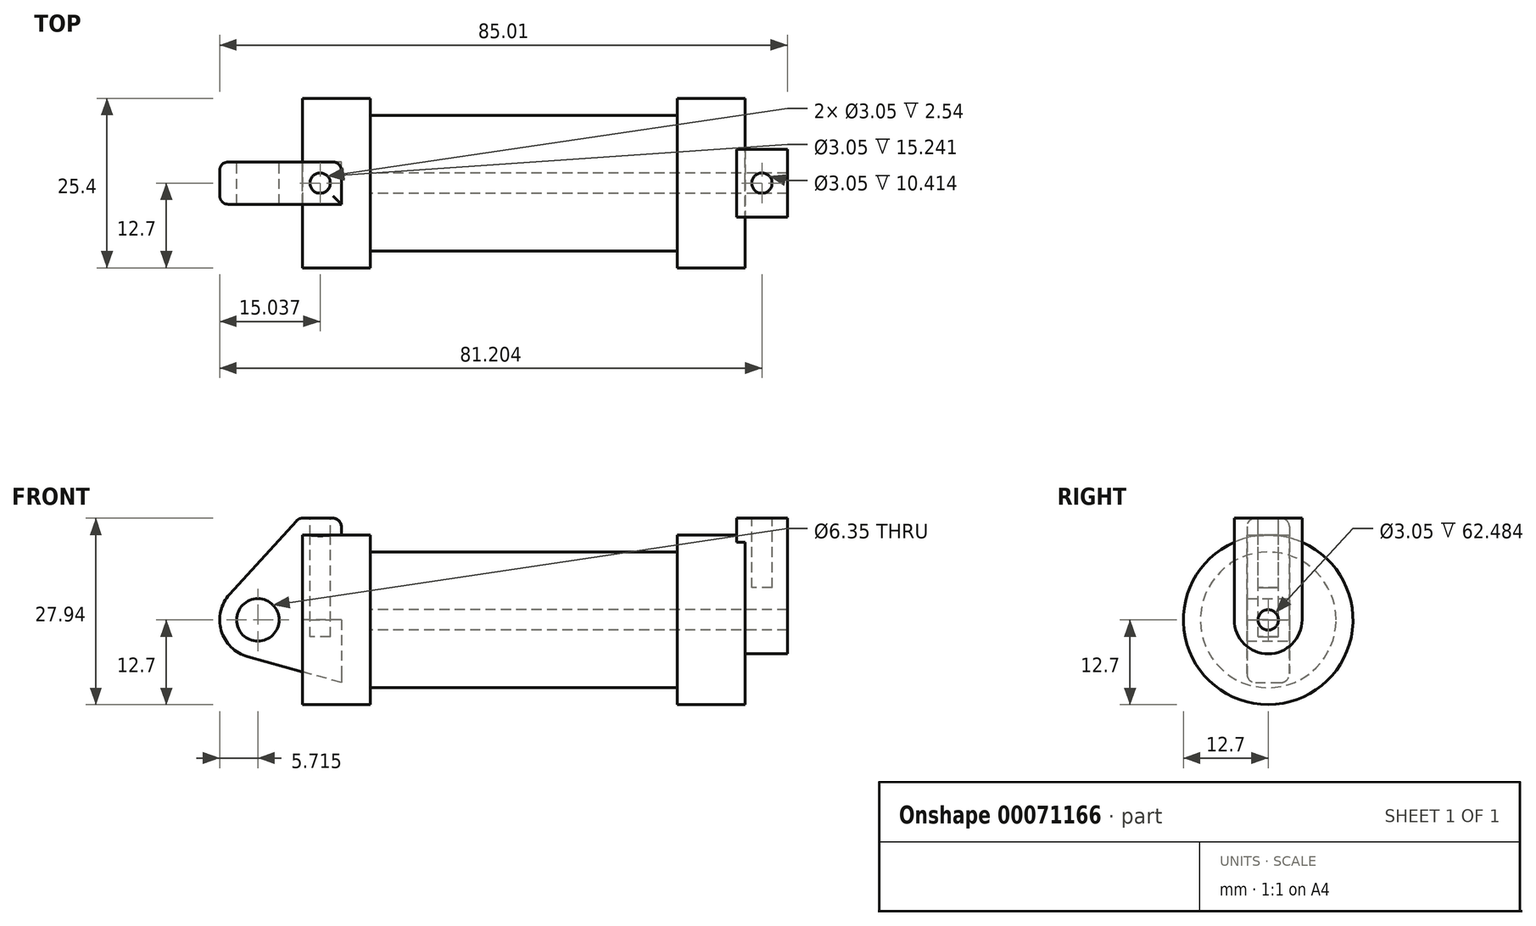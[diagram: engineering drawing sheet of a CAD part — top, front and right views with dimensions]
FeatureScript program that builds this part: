
annotation { "Feature Type Name" : "Feature", "Feature Type Description" : "" }
export const myFeature = defineFeature(function(context is Context, id is Id, definition is map)
    precondition{}
    {
        {
            var Q0;
            Q0=qCreatedBy(makeId("Front.planeOp"),FACE);
            var sketch = newSketch(context, id + "F0", { "sketchPlane" : qUnion([Q0])});
            skLineSegment(sketch, "E0", {"start": v(0, 0) * mm, "end": v(0, 12.7) * mm});
            skLineSegment(sketch, "E1", {"start": v(0, 12.7) * mm, "end": v(10.16, 12.7) * mm});
            skLineSegment(sketch, "E2", {"start": v(10.16, 12.7) * mm, "end": v(10.16, 10.16) * mm});
            skLineSegment(sketch, "E3", {"start": v(10.16, 10.16) * mm, "end": v(56.13, 10.16) * mm});
            skLineSegment(sketch, "E4", {"start": v(56.13, 10.16) * mm, "end": v(56.13, 12.7) * mm});
            skLineSegment(sketch, "E5", {"start": v(56.13, 12.7) * mm, "end": v(66.3, 12.7) * mm});
            skLineSegment(sketch, "E6", {"start": v(66.3, 12.7) * mm, "end": v(66.3, 0) * mm});
            skLineSegment(sketch, "E7", {"start": v(66.3, 0) * mm, "end": v(0, 0) * mm});
            skLineSegment(sketch, "E8", {"start": v(5.84, 15.24) * mm, "end": v(-0.5, 15.24) * mm});
            skLineSegment(sketch, "E9", {"start": v(-0.5, 15.24) * mm, "end": v(-10.88, 3.85) * mm});
            skLineSegment(sketch, "E10", {"start": v(0, 0) * mm, "end": v(-6.65, 0) * mm});
            skCircle(sketch, "E11", {"center": v(-6.65, 0) * mm, "radius": 5.72 * mm});
            skCircle(sketch, "E12", {"center": v(-6.65, 0) * mm, "radius": 3.18 * mm});
            skLineSegment(sketch, "E13", {"start": v(5.84, 15.24) * mm, "end": v(5.84, -9.4) * mm});
            skLineSegment(sketch, "E14", {"start": v(5.84, -9.4) * mm, "end": v(-8.18, -5.5) * mm});
            skSolve(sketch);
        }
        {
            var Q0;
            {var subQ0=sQuery(id+"F0.wireOp",EDGE,"E0");Q0=makeQuery(id+"F0.imprint","IMPRINT",FACE,{"disambiguationData":[TD([[makeQuery(id+"F0.imprint","IMPRINT",EDGE,{"derivedFrom":subQ0}),-1.0]])]});}
            var Q1;
            {var subQ0=sQuery(id+"F0.wireOp",EDGE,"E2");Q1=makeQuery(id+"F0.imprint","IMPRINT",FACE,{"disambiguationData":[TD([[makeQuery(id+"F0.imprint","IMPRINT",EDGE,{"derivedFrom":subQ0}),-1.0]])]});}
            var Q2;
            Q2=sQuery(id+"F0.wireOp",EDGE,"E7");
            revolve(context, id + "F1", {"entities" : qUnion([Q0, Q1]), "axis" : qUnion([Q2]), "revolveType" : RevolveType.FULL});
        }
        {
            var Q0;
            {var subQ3=sQuery(id+"F0.wireOp",EDGE,"E0");Q0=makeQuery(id+"F0.imprint","IMPRINT",FACE,{"disambiguationData":[TD([[makeQuery(id+"F0.imprint","IMPRINT",EDGE,{"derivedFrom":subQ3}),1.0]])]});}
            var Q1;
            {var subQ4=sQuery(id+"F0.wireOp",EDGE,"E12");Q1=makeQuery(id+"F0.imprint","IMPRINT",FACE,{"disambiguationData":[TD([[makeQuery(id+"F0.imprint","IMPRINT",EDGE,{"derivedFrom":subQ4}),-1.0]])]});}
            var Q2;
            {var subQ0=sQuery(id+"F0.wireOp",EDGE,"E14");Q2=makeQuery(id+"F0.imprint","IMPRINT",FACE,{"disambiguationData":[TD([[makeQuery(id+"F0.imprint","IMPRINT",EDGE,{"derivedFrom":subQ0}),-1.0]])]});}
            extrude(context, id + "F2", {"entities" : qUnion([Q0, Q1, Q2]), "endBound" : BoundingType.SYMMETRIC, "depth" : 6.35 * mm});
        }
        {
            var Q0;
            Q0=makeQuery(id+"F1.opRevolve","SWEPT_FACE",FACE,{"disambiguationData":[OSD([sQuery(id+"F0.wireOp",EDGE,"E6")])]});
            var sketch = newSketch(context, id + "F3", { "sketchPlane" : qUnion([Q0])});
            skCircle(sketch, "E15", {"center": v(0, 0) * mm, "radius": 5.08 * mm});
            skCircle(sketch, "E16", {"center": v(0, 0) * mm, "radius": 1.52 * mm});
            skLineSegment(sketch, "E17", {"start": v(-5.08, 0) * mm, "end": v(-5.08, 15.24) * mm});
            skLineSegment(sketch, "E18.bottom", {"start": v(-5.08, 15.24) * mm, "end": v(5.08, 15.24) * mm});
            skLineSegment(sketch, "E18.left", {"start": v(-5.08, 15.24) * mm, "end": v(-5.08, 0) * mm});
            skLineSegment(sketch, "E18.right", {"start": v(5.08, 15.24) * mm, "end": v(5.08, 0) * mm});
            skSolve(sketch);
        }
        {
            var Q0;
            Q0 = qSketchRegion(id + "F3", true);
            extrude(context, id + "F4", {"entities" : qUnion([Q0]), "operationType" : NewBodyOperationType.ADD, "depth" : 6.35 * mm, "hasSecondDirection" : true, "secondDirectionOppositeDirection" : true, "secondDirectionDepth" : 1.27 * mm});
        }
        {
            var Q0;
            Q0=makeQuery(id+"F4.boolean.opBoolean","SPLIT",FACE,{"disambiguationData":[TD([makeQuery(id+"F4.opExtrude","SWEPT_FACE",FACE,{"disambiguationData":[OSD([sQuery(id+"F3.wireOp",EDGE,"E16")])]})])],"derivedFrom":makeQuery(id+"F1.opRevolve","SWEPT_FACE",FACE,{"disambiguationData":[OSD([sQuery(id+"F0.wireOp",EDGE,"E6")])]})});
            var Q1;
            Q1=makeQuery(id+"F1.opRevolve","SWEPT_FACE",FACE,{"disambiguationData":[OSD([sQuery(id+"F0.wireOp",EDGE,"E2")])]});
            extrude(context, id + "F5", {"entities" : qUnion([Q0]), "operationType" : NewBodyOperationType.REMOVE, "endBound" : BoundingType.UP_TO_SURFACE, "oppositeDirection" : true, "endBoundEntityFace" : qUnion([Q1]), "depth" : 25.4 * mm});
        }
        {
            var Q0;
            Q0=makeQuery(id+"F2.opExtrude","SWEPT_FACE",FACE,{"disambiguationData":[OSD([sQuery(id+"F0.wireOp",EDGE,"E8")])]});
            var sketch = newSketch(context, id + "F6", { "sketchPlane" : qUnion([Q0])});
            skCircle(sketch, "E19", {"center": v(2.67, 0) * mm, "radius": 1.52 * mm});
            skPoint(sketch, "E20.orphan", {"position": v(5.84, 0) * mm});
            skPoint(sketch, "E21.orphan", {"position": v(2.67, 3.18) * mm});
            skPoint(sketch, "E22.orphan", {"position": v(2.67, -3.18) * mm});
            skSolve(sketch);
        }
        {
            var Q0;
            Q0 = qSketchRegion(id + "F6", true);
            extrude(context, id + "F7", {"entities" : qUnion([Q0]), "operationType" : NewBodyOperationType.REMOVE, "oppositeDirection" : true, "depth" : 17.78 * mm});
        }
        {
            var Q0;
            Q0=makeQuery(id+"F4.opExtrude","SWEPT_FACE",FACE,{"disambiguationData":[OSD([sQuery(id+"F3.wireOp",EDGE,"E18.bottom")])]});
            var sketch = newSketch(context, id + "F8", { "sketchPlane" : qUnion([Q0])});
            skCircle(sketch, "E23", {"center": v(68.83, 0) * mm, "radius": 1.52 * mm});
            skPoint(sketch, "E24.trimOffspring.end.orphan", {"position": v(68.83, -5.08) * mm});
            skPoint(sketch, "E25.trimOffspring.end.orphan", {"position": v(72.64, 0) * mm});
            skPoint(sketch, "E26.start.orphan", {"position": v(68.83, 5.08) * mm});
            skPoint(sketch, "E27.start.orphan", {"position": v(65.02, 0) * mm});
            skSolve(sketch);
        }
        {
            var Q0;
            Q0 = qSketchRegion(id + "F8", true);
            extrude(context, id + "F9", {"entities" : qUnion([Q0]), "operationType" : NewBodyOperationType.REMOVE, "oppositeDirection" : true, "depth" : 10.4 * mm});
        }
        {
            var Q0;
            Q0=makeQuery(id+"F1.opRevolve","SWEPT_EDGE",EDGE,{"disambiguationData":[OSD([sQuery(id+"F0.wireOp",EDGE,"E1"),sQuery(id+"F0.wireOp",EDGE,"E2")])]});
            var Q1;
            Q1=makeQuery(id+"F1.opRevolve","SWEPT_EDGE",EDGE,{"disambiguationData":[OSD([sQuery(id+"F0.wireOp",EDGE,"E0"),sQuery(id+"F0.wireOp",EDGE,"E1")])]});
            var Q2;
            Q2=makeQuery(id+"F1.opRevolve","SWEPT_EDGE",EDGE,{"disambiguationData":[OSD([sQuery(id+"F0.wireOp",EDGE,"E5"),sQuery(id+"F0.wireOp",EDGE,"E6")])]});
            var Q3;
            Q3=makeQuery(id+"F1.opRevolve","SWEPT_EDGE",EDGE,{"disambiguationData":[OSD([sQuery(id+"F0.wireOp",EDGE,"E4"),sQuery(id+"F0.wireOp",EDGE,"E5")])]});
            var Q4;
            Q4=makeQuery(id+"F4.opExtrude","CAP_EDGE",EDGE,{"disambiguationData":[OSD([sQuery(id+"F3.wireOp",EDGE,"E15")])],"isStart":false});
            var Q5;
            Q5=makeQuery(id+"F4.opExtrude","SWEPT_EDGE",EDGE,{"disambiguationData":[OSD([sQuery(id+"F3.wireOp",EDGE,"E18.bottom"),sQuery(id+"F3.wireOp",EDGE,"E18.left")])]});
            var Q6;
            Q6=makeQuery(id+"F4.opExtrude","CAP_EDGE",EDGE,{"disambiguationData":[OSD([sQuery(id+"F3.wireOp",EDGE,"E18.bottom")])],"isStart":false});
            var Q7;
            Q7=makeQuery(id+"F4.opExtrude","SWEPT_EDGE",EDGE,{"disambiguationData":[OSD([sQuery(id+"F3.wireOp",EDGE,"E18.bottom"),sQuery(id+"F3.wireOp",EDGE,"E18.right")])]});
            var Q8;
            Q8=makeQuery(id+"F4.opExtrude","CAP_EDGE",EDGE,{"disambiguationData":[OSD([sQuery(id+"F3.wireOp",EDGE,"E18.bottom")])],"isStart":true});
            var Q9;
            Q9=makeQuery(id+"F2.opExtrude","CAP_EDGE",EDGE,{"disambiguationData":[OSD([sQuery(id+"F0.wireOp",EDGE,"E8")])],"isStart":true});
            var Q10;
            Q10=makeQuery(id+"F2.opExtrude","SWEPT_EDGE",EDGE,{"disambiguationData":[OSD([sQuery(id+"F0.wireOp",EDGE,"E8"),sQuery(id+"F0.wireOp",EDGE,"E9")])]});
            var Q11;
            Q11=makeQuery(id+"F2.opExtrude","CAP_EDGE",EDGE,{"disambiguationData":[OSD([sQuery(id+"F0.wireOp",EDGE,"E8")])],"isStart":false});
            var Q12;
            Q12=makeQuery(id+"F2.opExtrude","SWEPT_EDGE",EDGE,{"disambiguationData":[OSD([sQuery(id+"F0.wireOp",EDGE,"E8"),sQuery(id+"F0.wireOp",EDGE,"E13")])]});
            var Q13;
            Q13=makeQuery(id+"F2.opExtrude","CAP_EDGE",EDGE,{"disambiguationData":[OSD([sQuery(id+"F0.wireOp",EDGE,"E9")])],"isStart":true});
            var Q14;
            Q14=makeQuery(id+"F2.opExtrude","CAP_EDGE",EDGE,{"disambiguationData":[OSD([sQuery(id+"F0.wireOp",EDGE,"E9")])],"isStart":false});
            var Q15;
            {var subQ0=sQuery(id+"F0.wireOp",EDGE,"E13");Q15=makeQuery(id+"F2.opExtrude","CAP_EDGE",EDGE,{"disambiguationData":[OSD([subQ0]),TDD([makeQuery(id+"F0.imprint","IMPRINT",EDGE,{"disambiguationData":[TD([[makeQuery(id+"F0.imprint","INTERSECT",VERTEX,{"derivedFrom":[sQuery(id+"F0.wireOp",EDGE,"E8"),subQ0]}),-1.0]])],"derivedFrom":subQ0})])],"isStart":true});}
            var Q16;
            Q16=makeQuery(id+"F4.opExtrude","CAP_EDGE",EDGE,{"disambiguationData":[OSD([sQuery(id+"F3.wireOp",EDGE,"E18.right")])],"isStart":true});
            var Q17;
            Q17=makeQuery(id+"F4.opExtrude","CAP_EDGE",EDGE,{"disambiguationData":[OSD([sQuery(id+"F3.wireOp",EDGE,"E18.left")])],"isStart":true});
            var Q18;
            Q18=makeQuery(id+"F4.boolean.opBoolean","INTERSECT",EDGE,{"derivedFrom":[makeQuery(id+"F1.opRevolve","SWEPT_FACE",FACE,{"disambiguationData":[OSD([sQuery(id+"F0.wireOp",EDGE,"E5")])]}),makeQuery(id+"F4.opExtrude","CAP_FACE",FACE,{"disambiguationData":[OSD([sQuery(id+"F3.wireOp",EDGE,"E15"),sQuery(id+"F3.wireOp",EDGE,"E16"),sQuery(id+"F3.wireOp",EDGE,"E18.bottom"),sQuery(id+"F3.wireOp",EDGE,"E18.left"),sQuery(id+"F3.wireOp",EDGE,"E18.right")])],"isStart":true})]});
            fillet(context, id + "F10", {"entities" : qUnion([Q0, Q1, Q2, Q3, Q4, Q5, Q6, Q7, Q8, Q9, Q10, Q11, Q12, Q13, Q14, Q15, Q16, Q17, Q18]), "radius" : 1.27 * mm, "tangentPropagation" : true, "allowEdgeOverflow" : false});
        }
    });
